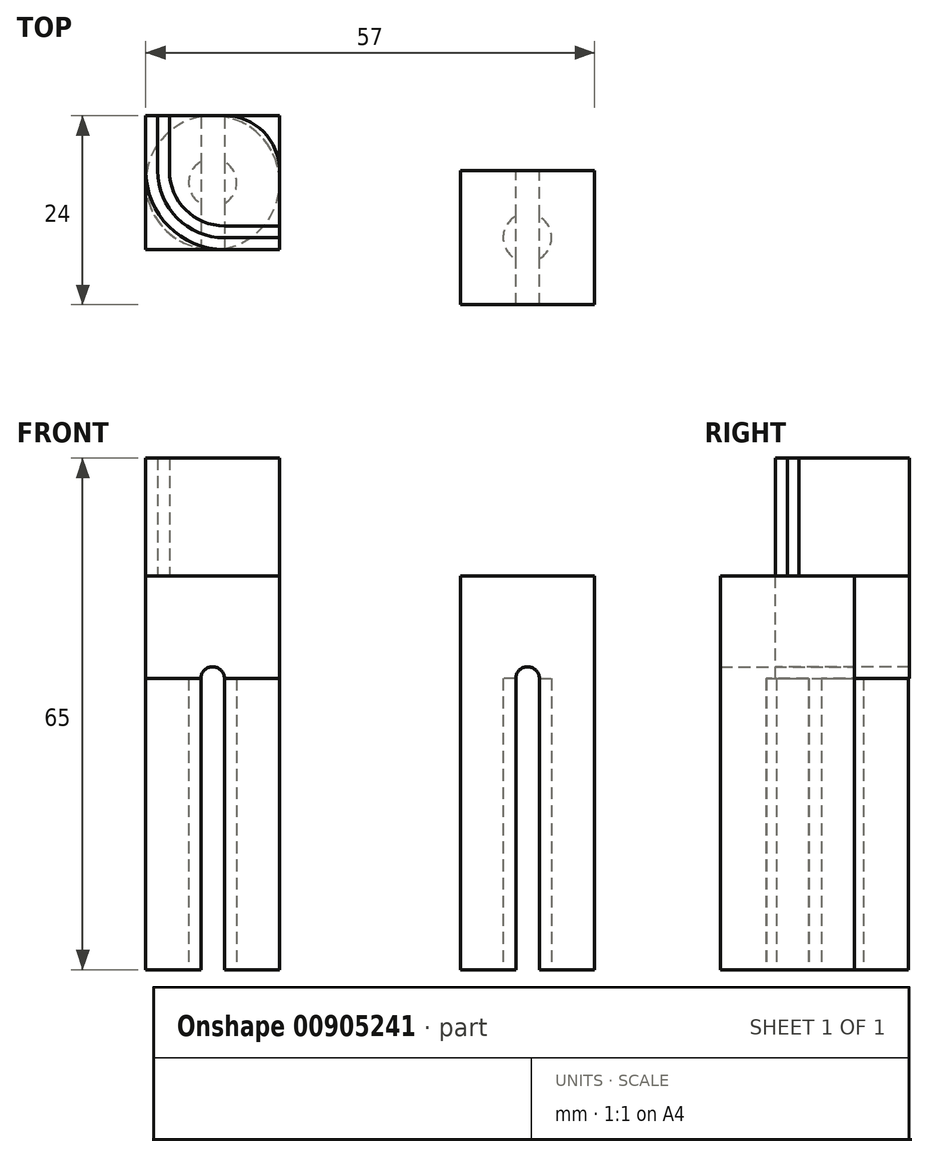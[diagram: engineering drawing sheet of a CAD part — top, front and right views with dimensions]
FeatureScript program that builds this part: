
annotation { "Feature Type Name" : "Feature", "Feature Type Description" : "" }
export const myFeature = defineFeature(function(context is Context, id is Id, definition is map)
    precondition{}
    {
        {
            var Q0;
            Q0=qCreatedBy(makeId("Top.planeOp"),FACE);
            var sketch = newSketch(context, id + "F0", { "sketchPlane" : qUnion([Q0])});
            skLineSegment(sketch, "E0.bottom", {"start": v(7, -10) * mm, "end": v(0, -10) * mm});
            skLineSegment(sketch, "E0.right", {"start": v(-10, 0) * mm, "end": v(-10, 7) * mm});
            skPoint(sketch, "E0.middle", {"position": v(0, 0) * mm});
            skArc(sketch, "E1.filletArc", {"start": v(-10, 0) * mm, "mid": v(-7.07, -7.07) * mm, "end": v(0, -10) * mm});
            skArc(sketch, "E2.0", {"start": v(-8.5, 0) * mm, "mid": v(-6.01, -6.01) * mm, "end": v(0, -8.5) * mm});
            skLineSegment(sketch, "E3", {"start": v(-8.5, 0) * mm, "end": v(-8.5, 7) * mm});
            skLineSegment(sketch, "E4", {"start": v(0, -8.5) * mm, "end": v(7, -8.5) * mm});
            skLineSegment(sketch, "E5.0", {"start": v(-7, 0) * mm, "end": v(-7, 7) * mm});
            skArc(sketch, "E5.1", {"start": v(-7, 0) * mm, "mid": v(-4.95, -4.95) * mm, "end": v(0, -7) * mm});
            skLineSegment(sketch, "E5.2", {"start": v(0, -7) * mm, "end": v(7, -7) * mm});
            skArc(sketch, "E6", {"start": v(7, 0) * mm, "mid": v(4.95, 4.95) * mm, "end": v(0, 7) * mm});
            skLineSegment(sketch, "E7", {"start": v(0, 7) * mm, "end": v(-7, 7) * mm});
            skLineSegment(sketch, "E8", {"start": v(7, 0) * mm, "end": v(7, -7) * mm});
            skLineSegment(sketch, "E9", {"start": v(7, -7) * mm, "end": v(7, -10) * mm});
            skLineSegment(sketch, "E10", {"start": v(-7, 7) * mm, "end": v(-10, 7) * mm});
            skPoint(sketch, "E11", {"position": v(7, -8.5) * mm});
            skPoint(sketch, "E12", {"position": v(-8.5, 0) * mm});
            skPoint(sketch, "E13", {"position": v(-7, 0) * mm});
            skPoint(sketch, "E14", {"position": v(-10, 0) * mm});
            skPoint(sketch, "E15", {"position": v(-8.5, 7) * mm});
            skSolve(sketch);
        }
        {
            var Q0;
            {var subQ1=sQuery(id+"F0.wireOp",EDGE,"E0.bottom");Q0=makeQuery(id+"F0.imprint","IMPRINT",FACE,{"disambiguationData":[TD([[makeQuery(id+"F0.imprint","IMPRINT",EDGE,{"derivedFrom":subQ1}),-1.0]])]});}
            var Q1;
            Q1=makeQuery(id+"F0.imprint","IMPRINT",FACE,{"disambiguationData":[TD([[makeQuery(id+"F0.imprint","IMPRINT",EDGE,{"derivedFrom":sQuery(id+"F0.wireOp",EDGE,"E5.0")}),-1.0]])]});
            extrude(context, id + "F1", {"entities" : qUnion([Q0, Q1]), "depth" : 15 * mm, "offsetDistance" : 25 * mm});
        }
        {
            var Q0;
            Q0=qCreatedBy(makeId("Front.planeOp"),FACE);
            var sketch = newSketch(context, id + "F2", { "sketchPlane" : qUnion([Q0])});
            skLineSegment(sketch, "E16.bottom", {"start": v(30, 0) * mm, "end": v(47, 0) * mm});
            skLineSegment(sketch, "E16.top", {"start": v(30, -50) * mm, "end": v(47, -50) * mm});
            skLineSegment(sketch, "E16.left", {"start": v(30, 0) * mm, "end": v(30, -50) * mm});
            skLineSegment(sketch, "E16.right", {"start": v(47, 0) * mm, "end": v(47, -50) * mm});
            skPoint(sketch, "E17", {"position": v(38.5, -50) * mm});
            skPoint(sketch, "E18", {"position": v(40, -50) * mm});
            skLineSegment(sketch, "E19.bottom", {"start": v(40, -50) * mm, "end": v(37, -50) * mm});
            skLineSegment(sketch, "E19.top", {"start": v(40, -13) * mm, "end": v(37, -13) * mm});
            skLineSegment(sketch, "E19.left", {"start": v(40, -50) * mm, "end": v(40, -13) * mm});
            skLineSegment(sketch, "E19.right", {"start": v(37, -50) * mm, "end": v(37, -13) * mm});
            skArc(sketch, "E20", {"start": v(40, -13) * mm, "mid": v(38.5, -11.5) * mm, "end": v(37, -13) * mm});
            skSolve(sketch);
        }
        {
            var Q0;
            Q0=makeQuery(id+"F2.imprint","IMPRINT",FACE,{"disambiguationData":[TD([[makeQuery(id+"F2.imprint","IMPRINT",EDGE,{"derivedFrom":sQuery(id+"F2.wireOp",EDGE,"E16.bottom")}),-1.0]])]});
            extrude(context, id + "F3", {"entities" : qUnion([Q0]), "depth" : 17 * mm, "offsetDistance" : 25 * mm});
        }
        {
            var Q0;
            {var subQ0=sQuery(id+"F2.wireOp",EDGE,"E16.top");Q0=makeQuery(id+"F3.opExtrude","SWEPT_FACE",FACE,{"disambiguationData":[OSD([subQ0]),TDD([makeQuery(id+"F2.imprint","IMPRINT",EDGE,{"disambiguationData":[TD([[makeQuery(id+"F2.imprint","INTERSECT",VERTEX,{"derivedFrom":[subQ0,sQuery(id+"F2.wireOp",EDGE,"E16.left")]}),-1.0]])],"derivedFrom":subQ0})])]});}
            var sketch = newSketch(context, id + "F4", { "sketchPlane" : qUnion([Q0])});
            skPoint(sketch, "E21", {"position": v(30, 8.5) * mm});
            skLineSegment(sketch, "E22", {"start": v(30, 8.5) * mm, "end": v(38.5, 8.5) * mm});
            skArc(sketch, "E23", {"start": v(38.5, 11.6) * mm, "mid": v(35.4, 8.5) * mm, "end": v(38.5, 5.4) * mm});
            skLineSegment(sketch, "E24", {"start": v(38.5, 11.6) * mm, "end": v(38.5, 5.4) * mm});
            skSolve(sketch);
        }
        {
            var Q0;
            {var subQ0=sQuery(id+"F4.wireOp",EDGE,"E23");var subQ1=sQuery(id+"F4.wireOp",EDGE,"E22");var subQ2=makeQuery(id+"F4.imprint","INTERSECT",VERTEX,{"derivedFrom":[subQ1,subQ0]});Q0=makeQuery(id+"F4.imprint","IMPRINT",FACE,{"disambiguationData":[TD([[makeQuery(id+"F4.imprint","IMPRINT",EDGE,{"disambiguationData":[TD([[subQ2,-1.0]])],"derivedFrom":subQ1}),1.0]])]});}
            var Q1;
            {var subQ0=sQuery(id+"F4.wireOp",EDGE,"E23");var subQ1=sQuery(id+"F4.wireOp",EDGE,"E22");var subQ2=makeQuery(id+"F4.imprint","INTERSECT",VERTEX,{"derivedFrom":[subQ1,subQ0]});Q1=makeQuery(id+"F4.imprint","IMPRINT",FACE,{"disambiguationData":[TD([[makeQuery(id+"F4.imprint","IMPRINT",EDGE,{"disambiguationData":[TD([[subQ2,-1.0]])],"derivedFrom":subQ1}),-1.0]])]});}
            extrude(context, id + "F5", {"entities" : qUnion([Q0, Q1]), "operationType" : NewBodyOperationType.REMOVE, "oppositeDirection" : true, "depth" : 37 * mm, "offsetDistance" : 25 * mm});
        }
        {
            var Q0;
            {var subQ0=sQuery(id+"F2.wireOp",EDGE,"E16.top");Q0=makeQuery(id+"F3.opExtrude","SWEPT_FACE",FACE,{"disambiguationData":[OSD([subQ0]),TDD([makeQuery(id+"F2.imprint","IMPRINT",EDGE,{"disambiguationData":[TD([[makeQuery(id+"F2.imprint","INTERSECT",VERTEX,{"derivedFrom":[subQ0,sQuery(id+"F2.wireOp",EDGE,"E16.right")]}),1.0]])],"derivedFrom":subQ0})])]});}
            var sketch = newSketch(context, id + "F6", { "sketchPlane" : qUnion([Q0])});
            skPoint(sketch, "E25", {"position": v(47, 8.5) * mm});
            skLineSegment(sketch, "E26", {"start": v(47, 8.5) * mm, "end": v(38.5, 8.5) * mm});
            skArc(sketch, "E27", {"start": v(38.5, 11.55) * mm, "mid": v(41.55, 8.5) * mm, "end": v(38.5, 5.45) * mm});
            skLineSegment(sketch, "E28", {"start": v(38.5, 5.45) * mm, "end": v(38.5, 11.55) * mm});
            skSolve(sketch);
        }
        {
            var Q0;
            {var subQ0=sQuery(id+"F6.wireOp",EDGE,"E27");var subQ1=sQuery(id+"F6.wireOp",EDGE,"E26");var subQ2=makeQuery(id+"F6.imprint","INTERSECT",VERTEX,{"derivedFrom":[subQ1,subQ0]});Q0=makeQuery(id+"F6.imprint","IMPRINT",FACE,{"disambiguationData":[TD([[makeQuery(id+"F6.imprint","IMPRINT",EDGE,{"disambiguationData":[TD([[subQ2,-1.0]])],"derivedFrom":subQ1}),-1.0]])]});}
            var Q1;
            {var subQ0=sQuery(id+"F6.wireOp",EDGE,"E27");var subQ1=sQuery(id+"F6.wireOp",EDGE,"E26");var subQ2=makeQuery(id+"F6.imprint","INTERSECT",VERTEX,{"derivedFrom":[subQ1,subQ0]});Q1=makeQuery(id+"F6.imprint","IMPRINT",FACE,{"disambiguationData":[TD([[makeQuery(id+"F6.imprint","IMPRINT",EDGE,{"disambiguationData":[TD([[subQ2,-1.0]])],"derivedFrom":subQ1}),1.0]])]});}
            extrude(context, id + "F7", {"entities" : qUnion([Q0, Q1]), "operationType" : NewBodyOperationType.REMOVE, "oppositeDirection" : true, "depth" : 37 * mm, "offsetDistance" : 25 * mm});
        }
        {
            var Q0;
            Q0=makeQuery(id+"F1.opExtrude","CAP_FACE",FACE,{"disambiguationData":[OSD([sQuery(id+"F0.wireOp",EDGE,"E0.bottom"),sQuery(id+"F0.wireOp",EDGE,"E0.right"),sQuery(id+"F0.wireOp",EDGE,"E1.filletArc"),sQuery(id+"F0.wireOp",EDGE,"E2.0"),sQuery(id+"F0.wireOp",EDGE,"E3"),sQuery(id+"F0.wireOp",EDGE,"E4"),sQuery(id+"F0.wireOp",EDGE,"E9"),sQuery(id+"F0.wireOp",EDGE,"E10")])],"isStart":true});
            var sketch = newSketch(context, id + "F8", { "sketchPlane" : qUnion([Q0])});
            skLineSegment(sketch, "E29.bottom", {"start": v(7, 10) * mm, "end": v(-10, 10) * mm});
            skLineSegment(sketch, "E29.top", {"start": v(7, -7) * mm, "end": v(-10, -7) * mm});
            skLineSegment(sketch, "E29.left", {"start": v(7, 10) * mm, "end": v(7, -7) * mm});
            skLineSegment(sketch, "E29.right", {"start": v(-10, 10) * mm, "end": v(-10, -7) * mm});
            skSolve(sketch);
        }
        {
            var Q0;
            Q0=makeQuery(id+"F8.imprint","IMPRINT",FACE,{"disambiguationData":[TD([[makeQuery(id+"F8.imprint","IMPRINT",EDGE,{"derivedFrom":makeQuery(id+"F1.opExtrude","CAP_EDGE",EDGE,{"disambiguationData":[OSD([sQuery(id+"F0.wireOp",EDGE,"E2.0")])],"isStart":true})}),-1.0]])]});
            var Q1;
            {var subQ1=makeQuery(id+"F1.opExtrude","CAP_EDGE",EDGE,{"disambiguationData":[OSD([sQuery(id+"F0.wireOp",EDGE,"E1.filletArc")])],"isStart":true});Q1=makeQuery(id+"F8.imprint","IMPRINT",FACE,{"disambiguationData":[TD([[makeQuery(id+"F8.imprint","IMPRINT",EDGE,{"derivedFrom":subQ1}),1.0]])]});}
            var Q2;
            {var subQ1=makeQuery(id+"F1.opExtrude","CAP_EDGE",EDGE,{"disambiguationData":[OSD([sQuery(id+"F0.wireOp",EDGE,"E1.filletArc")])],"isStart":true});Q2=makeQuery(id+"F8.imprint","IMPRINT",FACE,{"disambiguationData":[TD([[makeQuery(id+"F8.imprint","IMPRINT",EDGE,{"derivedFrom":subQ1}),-1.0]])]});}
            extrude(context, id + "F9", {"entities" : qUnion([Q0, Q1, Q2]), "depth" : 50 * mm, "offsetDistance" : 25 * mm});
        }
        {
            var Q0;
            Q0=makeQuery(id+"F9.opExtrude","SWEPT_FACE",FACE,{"disambiguationData":[OSD([sQuery(id+"F8.wireOp",EDGE,"E29.bottom")])]});
            var sketch = newSketch(context, id + "F10", { "sketchPlane" : qUnion([Q0])});
            skPoint(sketch, "E30", {"position": v(-1.5, -50) * mm});
            skLineSegment(sketch, "E31", {"start": v(-1.5, -50) * mm, "end": v(0, -50) * mm});
            skLineSegment(sketch, "E32.bottom", {"start": v(0, -50) * mm, "end": v(-3, -50) * mm});
            skLineSegment(sketch, "E32.top", {"start": v(0, -13) * mm, "end": v(-3, -13) * mm});
            skLineSegment(sketch, "E32.left", {"start": v(0, -50) * mm, "end": v(0, -13) * mm});
            skLineSegment(sketch, "E32.right", {"start": v(-3, -50) * mm, "end": v(-3, -13) * mm});
            skArc(sketch, "E33", {"start": v(0, -13) * mm, "mid": v(-1.5, -11.5) * mm, "end": v(-3, -13) * mm});
            skSolve(sketch);
        }
        {
            var Q0;
            Q0=makeQuery(id+"F10.imprint","IMPRINT",FACE,{"disambiguationData":[TD([[makeQuery(id+"F10.imprint","IMPRINT",EDGE,{"derivedFrom":sQuery(id+"F10.wireOp",EDGE,"E32.top")}),-1.0]])]});
            var Q1;
            Q1=makeQuery(id+"F10.imprint","IMPRINT",FACE,{"disambiguationData":[TD([[makeQuery(id+"F10.imprint","IMPRINT",EDGE,{"derivedFrom":sQuery(id+"F10.wireOp",EDGE,"E32.top")}),1.0]])]});
            extrude(context, id + "F11", {"entities" : qUnion([Q0, Q1]), "operationType" : NewBodyOperationType.REMOVE, "oppositeDirection" : true, "depth" : 17 * mm, "offsetDistance" : 25 * mm});
        }
        {
            var Q0;
            {var subQ0=sQuery(id+"F8.wireOp",EDGE,"E29.bottom");var subQ1=sQuery(id+"F8.wireOp",EDGE,"E29.right");var subQ2=sQuery(id+"F8.wireOp",EDGE,"E29.top");Q0=makeQuery(id+"F11.boolean.opBoolean","SPLIT",FACE,{"disambiguationData":[TD([makeQuery(id+"F9.opExtrude","SWEPT_FACE",FACE,{"disambiguationData":[OSD([subQ1])]})])],"derivedFrom":makeQuery(id+"F9.opExtrude","CAP_FACE",FACE,{"disambiguationData":[OSD([subQ0,subQ2,sQuery(id+"F8.wireOp",EDGE,"E29.left"),subQ1])],"isStart":false})});}
            var sketch = newSketch(context, id + "F12", { "sketchPlane" : qUnion([Q0])});
            skPoint(sketch, "E34", {"position": v(-10, 1.5) * mm});
            skLineSegment(sketch, "E35", {"start": v(-10, 1.5) * mm, "end": v(-1.5, 1.5) * mm});
            skArc(sketch, "E36", {"start": v(-1.5, 4.55) * mm, "mid": v(-4.55, 1.5) * mm, "end": v(-1.5, -1.55) * mm});
            skLineSegment(sketch, "E37", {"start": v(-1.5, -1.55) * mm, "end": v(-1.5, 4.55) * mm});
            skSolve(sketch);
        }
        {
            var Q0;
            {var subQ0=sQuery(id+"F12.wireOp",EDGE,"E36");var subQ1=sQuery(id+"F12.wireOp",EDGE,"E35");var subQ2=makeQuery(id+"F12.imprint","INTERSECT",VERTEX,{"derivedFrom":[subQ1,subQ0]});Q0=makeQuery(id+"F12.imprint","IMPRINT",FACE,{"disambiguationData":[TD([[makeQuery(id+"F12.imprint","IMPRINT",EDGE,{"disambiguationData":[TD([[subQ2,-1.0]])],"derivedFrom":subQ1}),1.0]])]});}
            var Q1;
            {var subQ0=sQuery(id+"F12.wireOp",EDGE,"E36");var subQ1=sQuery(id+"F12.wireOp",EDGE,"E35");var subQ2=makeQuery(id+"F12.imprint","INTERSECT",VERTEX,{"derivedFrom":[subQ1,subQ0]});Q1=makeQuery(id+"F12.imprint","IMPRINT",FACE,{"disambiguationData":[TD([[makeQuery(id+"F12.imprint","IMPRINT",EDGE,{"disambiguationData":[TD([[subQ2,-1.0]])],"derivedFrom":subQ1}),-1.0]])]});}
            extrude(context, id + "F13", {"entities" : qUnion([Q0, Q1]), "operationType" : NewBodyOperationType.REMOVE, "oppositeDirection" : true, "depth" : 37 * mm, "offsetDistance" : 25 * mm});
        }
        {
            var Q0;
            {var subQ0=sQuery(id+"F8.wireOp",EDGE,"E29.bottom");var subQ1=sQuery(id+"F8.wireOp",EDGE,"E29.top");var subQ2=sQuery(id+"F8.wireOp",EDGE,"E29.left");Q0=makeQuery(id+"F11.boolean.opBoolean","SPLIT",FACE,{"disambiguationData":[TD([makeQuery(id+"F9.opExtrude","SWEPT_FACE",FACE,{"disambiguationData":[OSD([subQ2])]})])],"derivedFrom":makeQuery(id+"F9.opExtrude","CAP_FACE",FACE,{"disambiguationData":[OSD([subQ0,subQ1,subQ2,sQuery(id+"F8.wireOp",EDGE,"E29.right")])],"isStart":false})});}
            var sketch = newSketch(context, id + "F14", { "sketchPlane" : qUnion([Q0])});
            skPoint(sketch, "E38", {"position": v(7, 1.5) * mm});
            skLineSegment(sketch, "E39", {"start": v(7, 1.5) * mm, "end": v(-1.5, 1.5) * mm});
            skArc(sketch, "E40", {"start": v(-1.5, 4.55) * mm, "mid": v(1.55, 1.5) * mm, "end": v(-1.5, -1.55) * mm});
            skSolve(sketch);
        }
        {
            var Q0;
            {var subQ0=sQuery(id+"F14.wireOp",EDGE,"E40");var subQ1=sQuery(id+"F14.wireOp",EDGE,"E39");var subQ2=makeQuery(id+"F14.imprint","INTERSECT",VERTEX,{"derivedFrom":[subQ1,subQ0]});Q0=makeQuery(id+"F14.imprint","IMPRINT",FACE,{"disambiguationData":[TD([[makeQuery(id+"F14.imprint","IMPRINT",EDGE,{"disambiguationData":[TD([[subQ2,-1.0]])],"derivedFrom":subQ1}),-1.0]])]});}
            var Q1;
            {var subQ0=sQuery(id+"F14.wireOp",EDGE,"E40");var subQ1=sQuery(id+"F14.wireOp",EDGE,"E39");var subQ2=makeQuery(id+"F14.imprint","INTERSECT",VERTEX,{"derivedFrom":[subQ1,subQ0]});Q1=makeQuery(id+"F14.imprint","IMPRINT",FACE,{"disambiguationData":[TD([[makeQuery(id+"F14.imprint","IMPRINT",EDGE,{"disambiguationData":[TD([[subQ2,-1.0]])],"derivedFrom":subQ1}),1.0]])]});}
            extrude(context, id + "F15", {"entities" : qUnion([Q0, Q1]), "operationType" : NewBodyOperationType.REMOVE, "oppositeDirection" : true, "depth" : 37 * mm, "offsetDistance" : 25 * mm});
        }
        {
            var Q0;
            {var subQ0=sQuery(id+"F8.wireOp",EDGE,"E29.bottom");var subQ1=sQuery(id+"F8.wireOp",EDGE,"E29.right");var subQ2=sQuery(id+"F8.wireOp",EDGE,"E29.top");Q0=makeQuery(id+"F11.boolean.opBoolean","SPLIT",FACE,{"disambiguationData":[TD([makeQuery(id+"F9.opExtrude","SWEPT_FACE",FACE,{"disambiguationData":[OSD([subQ1])]})])],"derivedFrom":makeQuery(id+"F9.opExtrude","CAP_FACE",FACE,{"disambiguationData":[OSD([subQ0,subQ2,sQuery(id+"F8.wireOp",EDGE,"E29.left"),subQ1])],"isStart":false})});}
            var sketch = newSketch(context, id + "F16", { "sketchPlane" : qUnion([Q0])});
            skPoint(sketch, "E41", {"position": v(-10, 1.5) * mm});
            skLineSegment(sketch, "E42", {"start": v(-10, 1.5) * mm, "end": v(-1.5, 1.5) * mm});
            skArc(sketch, "E43", {"start": v(-1.5, 10) * mm, "mid": v(-10, 1.5) * mm, "end": v(-1.5, -7) * mm});
            skSolve(sketch);
        }
        {
            var Q0;
            {var subQ1=sQuery(id+"F8.wireOp",EDGE,"E29.right");var subQ4=sQuery(id+"F8.wireOp",EDGE,"E29.bottom");var subQ11=makeQuery(id+"F11.boolean.opBoolean","SPLIT",EDGE,{"disambiguationData":[TD([makeQuery(id+"F9.opExtrude","SWEPT_FACE",FACE,{"disambiguationData":[OSD([subQ1])]})])],"derivedFrom":makeQuery(id+"F9.opExtrude","CAP_EDGE",EDGE,{"disambiguationData":[OSD([subQ4])],"isStart":false})});Q0=makeQuery(id+"F16.imprint","IMPRINT",FACE,{"disambiguationData":[TD([[makeQuery(id+"F16.imprint","IMPRINT",EDGE,{"derivedFrom":subQ11}),1.0]])]});}
            var Q1;
            {var subQ1=sQuery(id+"F8.wireOp",EDGE,"E29.right");var subQ4=sQuery(id+"F8.wireOp",EDGE,"E29.top");var subQ12=makeQuery(id+"F11.boolean.opBoolean","SPLIT",EDGE,{"disambiguationData":[TD([makeQuery(id+"F9.opExtrude","SWEPT_FACE",FACE,{"disambiguationData":[OSD([subQ1])]})])],"derivedFrom":makeQuery(id+"F9.opExtrude","CAP_EDGE",EDGE,{"disambiguationData":[OSD([subQ4])],"isStart":false})});Q1=makeQuery(id+"F16.imprint","IMPRINT",FACE,{"disambiguationData":[TD([[makeQuery(id+"F16.imprint","IMPRINT",EDGE,{"derivedFrom":subQ12}),-1.0]])]});}
            extrude(context, id + "F17", {"entities" : qUnion([Q0, Q1]), "operationType" : NewBodyOperationType.REMOVE, "oppositeDirection" : true, "depth" : 37 * mm, "offsetDistance" : 25 * mm});
        }
        {
            var Q0;
            {var subQ0=sQuery(id+"F8.wireOp",EDGE,"E29.bottom");var subQ1=sQuery(id+"F8.wireOp",EDGE,"E29.top");var subQ2=sQuery(id+"F8.wireOp",EDGE,"E29.left");Q0=makeQuery(id+"F11.boolean.opBoolean","SPLIT",FACE,{"disambiguationData":[TD([makeQuery(id+"F9.opExtrude","SWEPT_FACE",FACE,{"disambiguationData":[OSD([subQ2])]})])],"derivedFrom":makeQuery(id+"F9.opExtrude","CAP_FACE",FACE,{"disambiguationData":[OSD([subQ0,subQ1,subQ2,sQuery(id+"F8.wireOp",EDGE,"E29.right")])],"isStart":false})});}
            var sketch = newSketch(context, id + "F18", { "sketchPlane" : qUnion([Q0])});
            skPoint(sketch, "E44", {"position": v(7, 1.5) * mm});
            skLineSegment(sketch, "E45", {"start": v(7, 1.5) * mm, "end": v(-1.5, 1.5) * mm});
            skArc(sketch, "E46", {"start": v(-1.5, 10) * mm, "mid": v(7, 1.5) * mm, "end": v(-1.5, -7) * mm});
            skSolve(sketch);
        }
        {
            var Q0;
            {var subQ1=sQuery(id+"F8.wireOp",EDGE,"E29.left");var subQ4=sQuery(id+"F8.wireOp",EDGE,"E29.bottom");var subQ11=makeQuery(id+"F11.boolean.opBoolean","SPLIT",EDGE,{"disambiguationData":[TD([makeQuery(id+"F9.opExtrude","SWEPT_FACE",FACE,{"disambiguationData":[OSD([subQ1])]})])],"derivedFrom":makeQuery(id+"F9.opExtrude","CAP_EDGE",EDGE,{"disambiguationData":[OSD([subQ4])],"isStart":false})});Q0=makeQuery(id+"F18.imprint","IMPRINT",FACE,{"disambiguationData":[TD([[makeQuery(id+"F18.imprint","IMPRINT",EDGE,{"derivedFrom":subQ11}),1.0]])]});}
            var Q1;
            {var subQ1=sQuery(id+"F8.wireOp",EDGE,"E29.left");var subQ4=sQuery(id+"F8.wireOp",EDGE,"E29.top");var subQ12=makeQuery(id+"F11.boolean.opBoolean","SPLIT",EDGE,{"disambiguationData":[TD([makeQuery(id+"F9.opExtrude","SWEPT_FACE",FACE,{"disambiguationData":[OSD([subQ1])]})])],"derivedFrom":makeQuery(id+"F9.opExtrude","CAP_EDGE",EDGE,{"disambiguationData":[OSD([subQ4])],"isStart":false})});Q1=makeQuery(id+"F18.imprint","IMPRINT",FACE,{"disambiguationData":[TD([[makeQuery(id+"F18.imprint","IMPRINT",EDGE,{"derivedFrom":subQ12}),-1.0]])]});}
            extrude(context, id + "F19", {"entities" : qUnion([Q0, Q1]), "operationType" : NewBodyOperationType.REMOVE, "oppositeDirection" : true, "depth" : 37 * mm, "offsetDistance" : 25 * mm});
        }
    });
